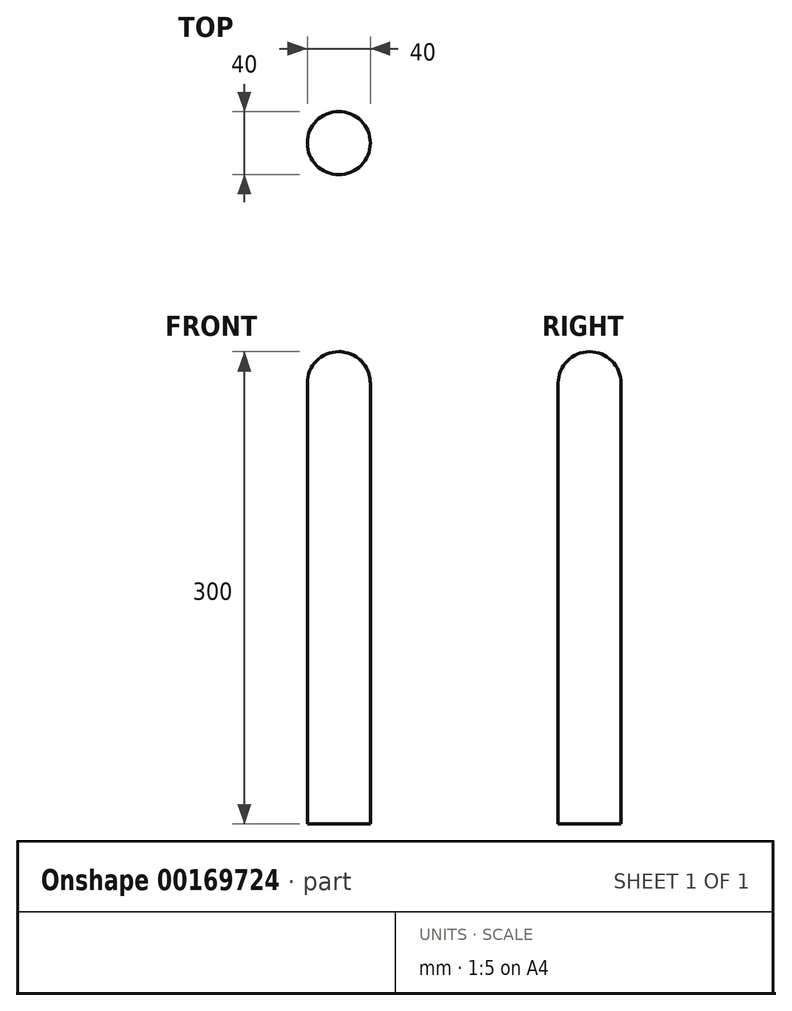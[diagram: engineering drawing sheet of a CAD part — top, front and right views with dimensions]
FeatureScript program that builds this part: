
annotation { "Feature Type Name" : "Feature", "Feature Type Description" : "" }
export const myFeature = defineFeature(function(context is Context, id is Id, definition is map)
    precondition{}
    {
        {
            var Q0;
            Q0=qCreatedBy(makeId("Top.planeOp"),FACE);
            var sketch = newSketch(context, id + "F0", { "sketchPlane" : qUnion([Q0])});
            skCircle(sketch, "E0", {"center": v(0, 0) * mm, "radius": 20 * mm});
            skSolve(sketch);
        }
        {
            var Q0;
            Q0=qSketchRegion(id+"F0",true);
            extrude(context, id + "F1", {"entities" : qUnion([Q0]), "depth" : 300 * mm});
        }
        {
            var Q0;
            Q0=makeQuery(id+"F1.opExtrude","CAP_EDGE",EDGE,{"disambiguationData":[OSD([sQuery(id+"F0.wireOp",EDGE,"E0")])],"isStart":false});
            fillet(context, id + "F2", {"entities" : qUnion([Q0]), "radius" : 20 * mm, "tangentPropagation" : true, "allowEdgeOverflow" : false});
        }
    });
